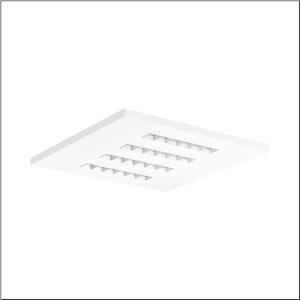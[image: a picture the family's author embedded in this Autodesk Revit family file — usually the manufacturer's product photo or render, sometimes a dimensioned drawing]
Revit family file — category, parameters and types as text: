
# Revit family: silica_21_square_51mx6mdu44w
name_source: partatom
category: Lighting Fixtures
units: mm (PartAtom-declared; Revit-internal decimal feet)

## family parameters
Cut with Voids When Loaded = No
Host = Face
Light Source = No
Part Type = Normal
Room Calculation Point = No
Round Connector Dimension = Use Diameter
Shared = No

## types (1)
- --- (1 x LED, 4600 lm, 27.2 W, 4000K)
    Apparent Load = 27 VA
    CIE Flux Codes = 83 98 100 100 100
    Color Rendering = 80
    Color Temperature = 4000K
    Default Elevation = 1800 mm
    Description = Silica 21 Square, office luminaire, primary light control with lens, of PMMA, primary anti-glare with reflector, of PC, white, CAT 2 (L<= 3000cd/m²), light emission: direct distribution, primary light characteristic: symmetric, installation type: lay-in mounting, LED, rated luminous flux: 4.600lm, luminous efficacy: 169lm/W, light colour: 840, colour temperature: 4000K, control gear: DALI 2, with terminal, 5-pole, mains connection: 220..240V, AC, 50/60Hz, rated input power: 27.2W, luminaire housing, of sheet steel, coated, traffic white (RAL 9016), module: M625, length: 622mm, width: 622mm, height: 33mm, protection rating (complete): IP20, insulation class (complete): insulation class I (protective earthing), certification: CE, ENEC, VDE, permissible operating ambient temperature: -20..+40°C, standard: EN 50419, packaging unit: 1 piece
    Height = 0 mm  [stored 0 ft]
    Lamp = 1 x LED
    Lamp Light Flux = 4600 lm
    Lamp Power = 27.2 W
    Lamp count = 1
    Length = 622 mm
    Luminous efficacy = 169 lm/W
    Manufacturer = Siteco
    ModVariant = No
    Model = 51MX6MDU44W
    Mounting Place = Ceiling
    Mounting Type = Recessed
    Number of Poles = 1
    OnlyDefault = Yes
    Power Factor = 1
    Product Name = Silica 21 Square
    Product group = office luminaire | ceiling recessed
    ProductGroupID = 400
    Protection Class = Protection class I
    Protection Degree = IP 20
    RLX_Detail_Level = 1
    RLX_Emergency_Light_Flux = 0 lm
    RLX_Emergency_Type = 0
    RLX_Emergency_Type_DB = No
    RlxData = <blob elided: 18633 chars, md5=e96b7c79>
    Socket = socket
    Standby Power = 0 W
    System Light Flux = 4600 lm
    System Power = 27 W
    Type Comments = factory setting: luminous flux: 100 % | dim-lin: 254 | 366 mA
    Type Image = l_1275220.jpg
    URL = http://relux.com
    VarID = @adj_090299
    Voltage = 0 V
    Weight = 0.00 kg
    Width = 622 mm

note: [stored X ft] marks values corroborated as IEEE doubles in the binary element streams (Revit-internal decimal feet)

## geometry (parser evidence)
native form markers: Blend x4, Sweep x13
no freeform markers — native parametric forms only
